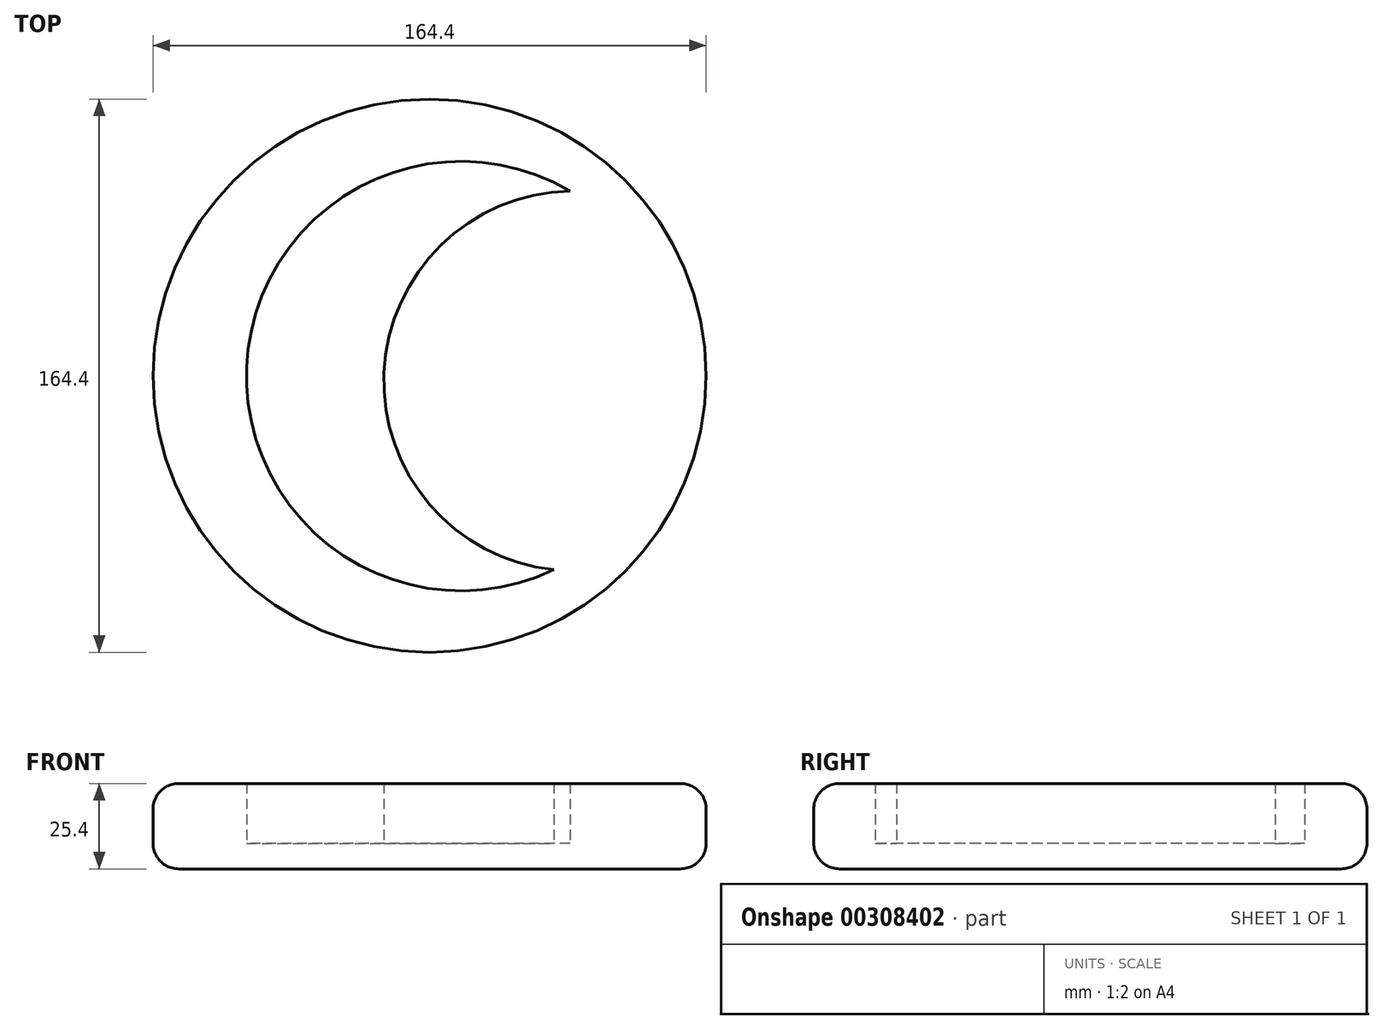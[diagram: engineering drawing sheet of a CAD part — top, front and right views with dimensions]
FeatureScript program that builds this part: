
annotation { "Feature Type Name" : "Feature", "Feature Type Description" : "" }
export const myFeature = defineFeature(function(context is Context, id is Id, definition is map)
    precondition{}
    {
        {
            var Q0;
            Q0=qCreatedBy(makeId("Top.planeOp"),FACE);
            var sketch = newSketch(context, id + "F0", { "sketchPlane" : qUnion([Q0])});
            skCircle(sketch, "E0", {"center": v(0, 0) * mm, "radius": 75.17 * mm});
            skArc(sketch, "E1", {"start": v(41.77, 54.91) * mm, "mid": v(-13.54, 0.87) * mm, "end": v(37, -57.65) * mm});
            skArc(sketch, "E2", {"start": v(41.77, 54.91) * mm, "mid": v(-54.36, 2.6) * mm, "end": v(37, -57.65) * mm});
            skCircle(sketch, "E3", {"center": v(0, 0) * mm, "radius": 82.2 * mm});
            skSolve(sketch);
        }
        {
            var Q0;
            Q0 = qSketchRegion(id + "F0", true);
            var Q1;
            Q1=makeQuery(id+"F0.imprint","IMPRINT",FACE,{"disambiguationData":[TD([[makeQuery(id+"F0.imprint","IMPRINT",EDGE,{"derivedFrom":sQuery(id+"F0.wireOp",EDGE,"E0")}),1.0]])]});
            extrude(context, id + "F1", {"entities" : qUnion([Q0, Q1]), "depth" : 25.4 * mm});
        }
        {
            var Q0;
            Q0=makeQuery(id+"F1.opExtrude","CAP_EDGE",EDGE,{"disambiguationData":[OSD([sQuery(id+"F0.wireOp",EDGE,"E3")])],"isStart":false});
            var Q1;
            Q1=makeQuery(id+"F1.opExtrude","CAP_EDGE",EDGE,{"disambiguationData":[OSD([sQuery(id+"F0.wireOp",EDGE,"E3")])],"isStart":true});
            fillet(context, id + "F2", {"entities" : qUnion([Q0, Q1]), "radius" : 7.62 * mm, "tangentPropagation" : true, "allowEdgeOverflow" : false});
        }
        {
            var Q0;
            Q0=makeQuery(id+"F0.imprint","IMPRINT",FACE,{"disambiguationData":[TD([[makeQuery(id+"F0.imprint","IMPRINT",EDGE,{"derivedFrom":sQuery(id+"F0.wireOp",EDGE,"E1")}),-1.0]])]});
            extrude(context, id + "F3", {"entities" : qUnion([Q0]), "operationType" : NewBodyOperationType.ADD, "depth" : 7.62 * mm});
        }
    });
